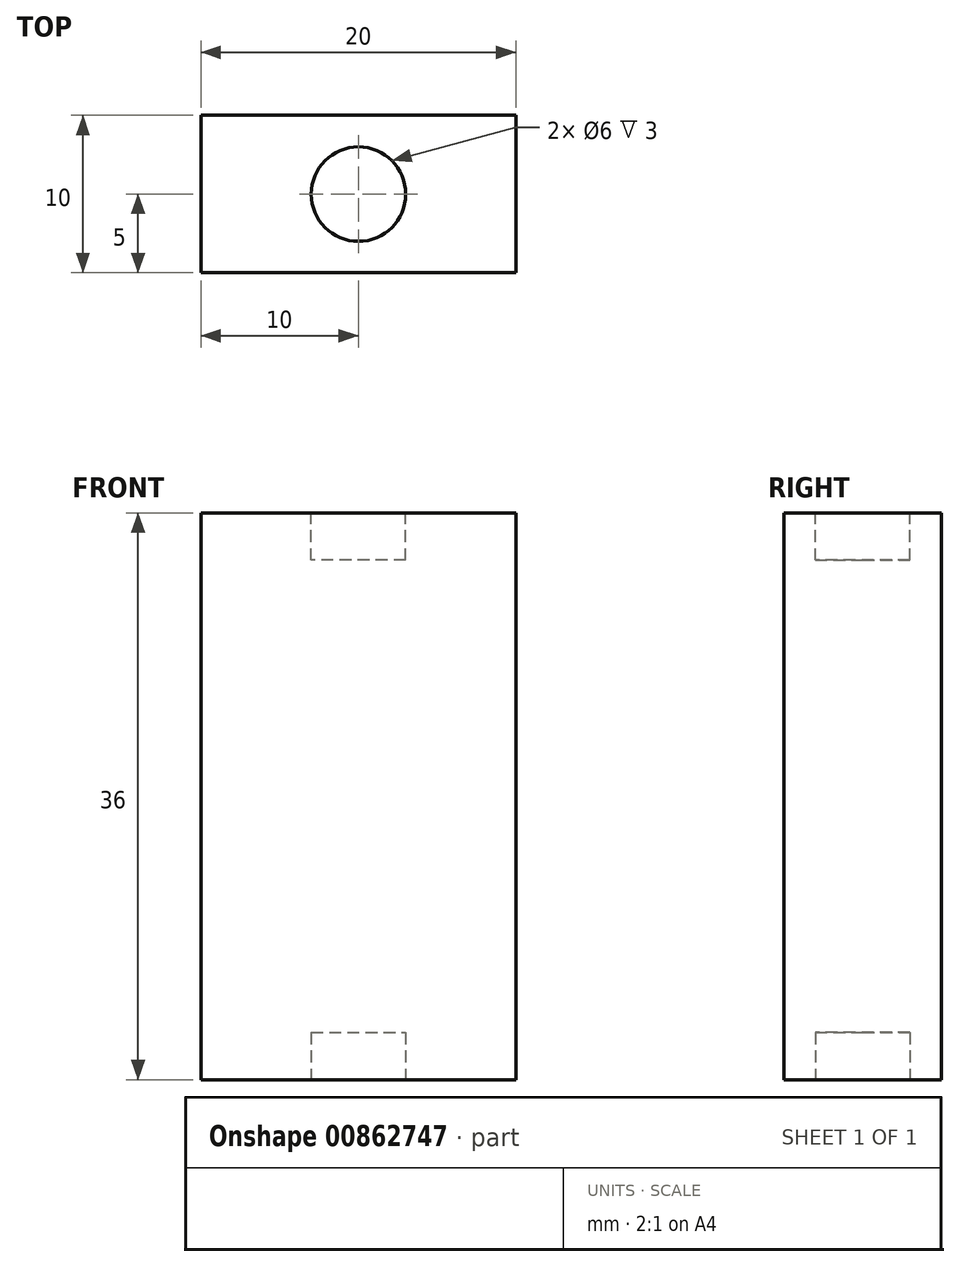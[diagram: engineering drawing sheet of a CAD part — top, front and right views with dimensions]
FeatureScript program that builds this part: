
annotation { "Feature Type Name" : "Feature", "Feature Type Description" : "" }
export const myFeature = defineFeature(function(context is Context, id is Id, definition is map)
    precondition{}
    {
        {
            var Q0;
            Q0=qCreatedBy(makeId("Front.planeOp"),FACE);
            var sketch = newSketch(context, id + "F0", { "sketchPlane" : qUnion([Q0])});
            skLineSegment(sketch, "E0", {"start": v(0, 0) * mm, "end": v(0, 36) * mm});
            skLineSegment(sketch, "E1", {"start": v(0, 36) * mm, "end": v(20, 36) * mm});
            skLineSegment(sketch, "E2", {"start": v(20, 36) * mm, "end": v(20, 0) * mm});
            skLineSegment(sketch, "E3", {"start": v(20, 0) * mm, "end": v(0, 0) * mm});
            skSolve(sketch);
        }
        {
            var Q0;
            Q0=makeQuery(id+"F0.imprint","IMPRINT",FACE,{"disambiguationData":[TD([[makeQuery(id+"F0.imprint","IMPRINT",EDGE,{"derivedFrom":sQuery(id+"F0.wireOp",EDGE,"E0")}),-1.0]])]});
            extrude(context, id + "F1", {"entities" : qUnion([Q0]), "depth" : 10 * mm, "offsetDistance" : 25 * mm});
        }
        {
            var Q0;
            Q0=makeQuery(id+"F1.opExtrude","SWEPT_FACE",FACE,{"disambiguationData":[OSD([sQuery(id+"F0.wireOp",EDGE,"E3")])]});
            var sketch = newSketch(context, id + "F2", { "sketchPlane" : qUnion([Q0])});
            skCircle(sketch, "E4", {"center": v(10, 5) * mm, "radius": 3 * mm});
            skSolve(sketch);
        }
        {
            var Q0;
            Q0=makeQuery(id+"F2.imprint","IMPRINT",FACE,{"disambiguationData":[TD([[makeQuery(id+"F2.imprint","IMPRINT",EDGE,{"derivedFrom":sQuery(id+"F2.wireOp",EDGE,"E4")}),1.0]])]});
            extrude(context, id + "F3", {"entities" : qUnion([Q0]), "operationType" : NewBodyOperationType.REMOVE, "oppositeDirection" : true, "depth" : 3 * mm, "offsetDistance" : 25 * mm});
        }
        {
            var Q0;
            Q0=makeQuery(id+"F1.opExtrude","SWEPT_FACE",FACE,{"disambiguationData":[OSD([sQuery(id+"F0.wireOp",EDGE,"E1")])]});
            var sketch = newSketch(context, id + "F4", { "sketchPlane" : qUnion([Q0])});
            skCircle(sketch, "E5", {"center": v(10, -5) * mm, "radius": 3 * mm});
            skSolve(sketch);
        }
        {
            var Q0;
            Q0=makeQuery(id+"F4.imprint","IMPRINT",FACE,{"disambiguationData":[TD([[makeQuery(id+"F4.imprint","IMPRINT",EDGE,{"derivedFrom":sQuery(id+"F4.wireOp",EDGE,"E5")}),1.0]])]});
            var Q1;
            Q1=sQuery(id+"F4.wireOp",EDGE,"E5");
            extrude(context, id + "F5", {"entities" : qUnion([Q0]), "operationType" : NewBodyOperationType.REMOVE, "surfaceEntities" : qUnion([Q1]), "oppositeDirection" : true, "depth" : 3 * mm, "offsetDistance" : 25 * mm});
        }
    });
